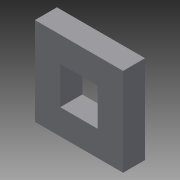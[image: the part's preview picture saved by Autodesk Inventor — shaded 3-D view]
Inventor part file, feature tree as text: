
AUTODESK INVENTOR PART (.ipt)
format: ipt  version: 2015 (Build 190159000, 159)  size: 75,264 bytes
history: native  units: mm
features: extrude x1, sketch x1
ambient origin geometry x8: Origin, YZ Plane, XZ Plane, XY Plane, X Axis, Y Axis, Z Axis, Center Point
bodies: Solid1 (feature_tree)
feature tree (2):
  extrude  "Extrusion1"  Depth=20.0mm
  sketch  "Sketch1"  dims[d0=20.0mm d1=20.0mm d2=8.5mm d3=8.5mm d4=5.0mm d5=0.0mm]
